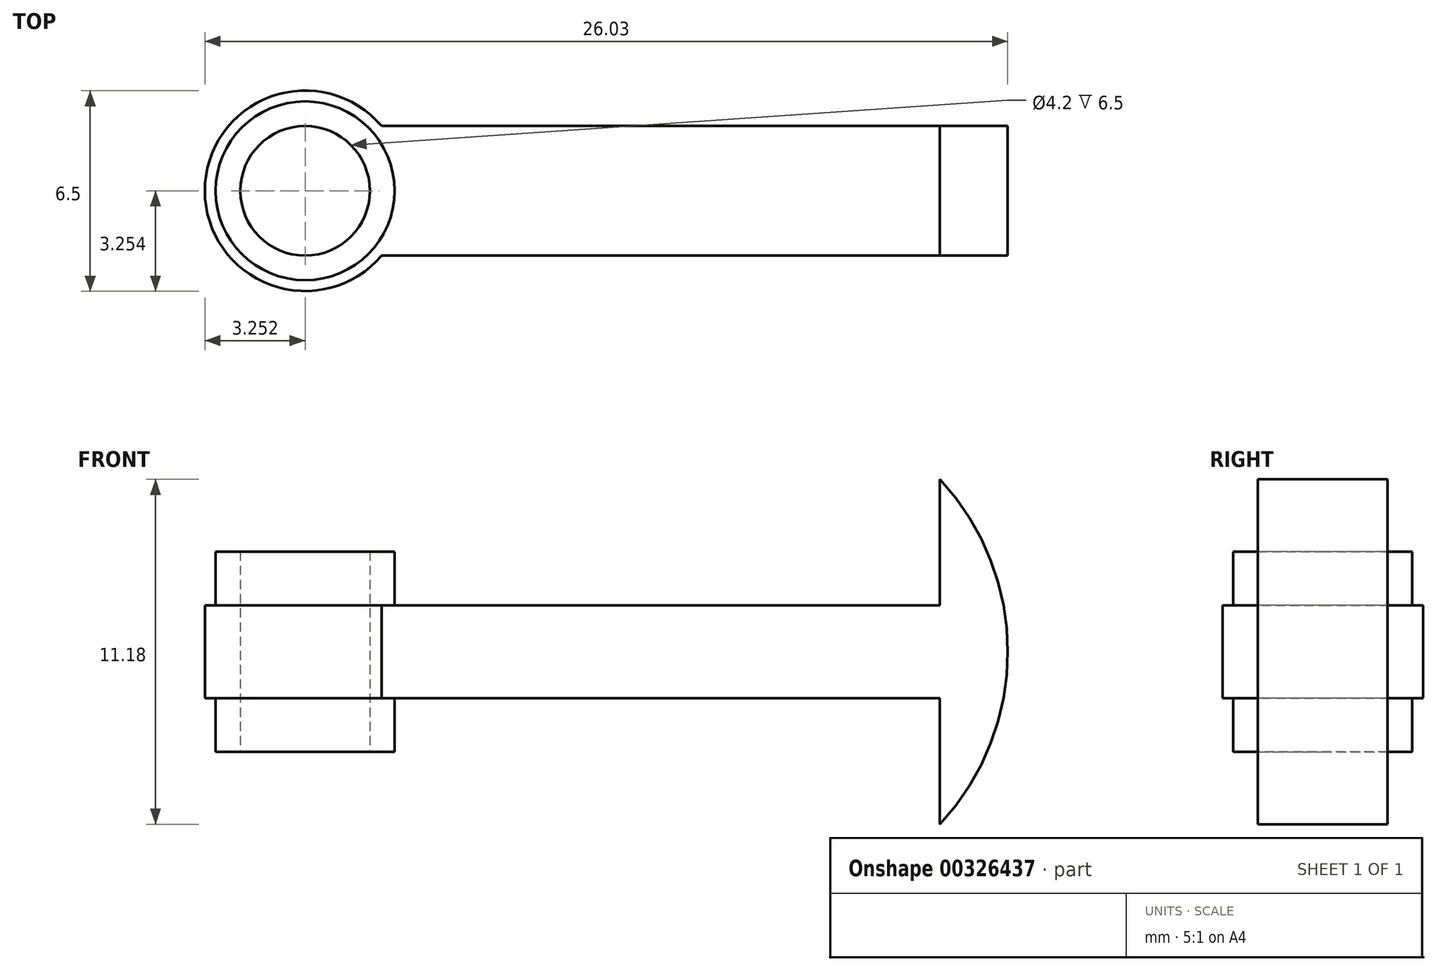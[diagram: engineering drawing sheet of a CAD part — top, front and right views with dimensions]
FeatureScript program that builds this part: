
annotation { "Feature Type Name" : "Feature", "Feature Type Description" : "" }
export const myFeature = defineFeature(function(context is Context, id is Id, definition is map)
    precondition{}
    {
        {
            var Q0;
            Q0=qCreatedBy(makeId("Top.planeOp"),FACE);
            var sketch = newSketch(context, id + "F0", { "sketchPlane" : qUnion([Q0])});
            skLineSegment(sketch, "E0.right", {"start": v(10.92, 10.5) * mm, "end": v(10.92, 8.1) * mm});
            skPoint(sketch, "E1", {"position": v(-5.16, 1.5) * mm});
            skPoint(sketch, "E2", {"position": v(-9.66, 6) * mm});
            skCircle(sketch, "E3", {"center": v(-9.66, 6) * mm, "radius": 2.1 * mm});
            skArc(sketch, "E4", {"start": v(-7.18, 8.1) * mm, "mid": v(-12.9, 6) * mm, "end": v(-7.18, 3.9) * mm});
            skLineSegment(sketch, "E5", {"start": v(-7.18, 8.1) * mm, "end": v(10.92, 8.1) * mm});
            skLineSegment(sketch, "E6", {"start": v(-7.18, 3.9) * mm, "end": v(10.92, 3.9) * mm});
            skPoint(sketch, "E0.left.start.orphan", {"position": v(-14.16, 10.5) * mm});
            skPoint(sketch, "E7.orphan", {"position": v(-14.16, 1.5) * mm});
            skLineSegment(sketch, "E8.bottom", {"start": v(10.92, 10.5) * mm, "end": v(18.8, 10.5) * mm});
            skLineSegment(sketch, "E8.top", {"start": v(10.92, 1.5) * mm, "end": v(18.8, 1.5) * mm});
            skLineSegment(sketch, "E8.right", {"start": v(18.8, 10.5) * mm, "end": v(18.8, 1.5) * mm});
            skLineSegment(sketch, "E9.trimOffspring", {"start": v(10.92, 3.9) * mm, "end": v(10.92, 1.5) * mm});
            skLineSegment(sketch, "E10", {"start": v(10.92, 8.1) * mm, "end": v(10.92, 3.9) * mm});
            skSolve(sketch);
        }
        {
            var Q0;
            Q0=makeQuery(id+"F0.imprint","IMPRINT",FACE,{"disambiguationData":[TD([[makeQuery(id+"F0.imprint","IMPRINT",EDGE,{"derivedFrom":sQuery(id+"F0.wireOp",EDGE,"E0.right")}),1.0]])]});
            var Q1;
            Q1=makeQuery(id+"F0.imprint","IMPRINT",FACE,{"disambiguationData":[TD([[makeQuery(id+"F0.imprint","IMPRINT",EDGE,{"derivedFrom":sQuery(id+"F0.wireOp",EDGE,"E3")}),-1.0]])]});
            extrude(context, id + "F1", {"entities" : qUnion([Q0, Q1]), "depth" : 3 * mm});
        }
        {
            var Q0;
            Q0=makeQuery(id+"F1.opExtrude","CAP_FACE",FACE,{"disambiguationData":[OSD([sQuery(id+"F0.wireOp",EDGE,"E0.right"),sQuery(id+"F0.wireOp",EDGE,"E3"),sQuery(id+"F0.wireOp",EDGE,"E4"),sQuery(id+"F0.wireOp",EDGE,"E5"),sQuery(id+"F0.wireOp",EDGE,"E6"),sQuery(id+"F0.wireOp",EDGE,"E8.bottom"),sQuery(id+"F0.wireOp",EDGE,"E8.top"),sQuery(id+"F0.wireOp",EDGE,"E8.right"),sQuery(id+"F0.wireOp",EDGE,"E9.trimOffspring")])],"isStart":false});
            var sketch = newSketch(context, id + "F2", { "sketchPlane" : qUnion([Q0])});
            skPoint(sketch, "E11", {"position": v(9.92, 10.5) * mm});
            skLineSegment(sketch, "E12", {"start": v(10.92, 8.1) * mm, "end": v(10.92, 3.9) * mm});
            skLineSegment(sketch, "E13", {"start": v(10.92, 3.9) * mm, "end": v(18.8, 3.9) * mm});
            skLineSegment(sketch, "E14", {"start": v(10.92, 8.1) * mm, "end": v(18.8, 8.1) * mm});
            skSolve(sketch);
        }
        {
            var Q0;
            {var subQ0=sQuery(id+"F2.wireOp",EDGE,"E14");Q0=makeQuery(id+"F2.imprint","IMPRINT",FACE,{"disambiguationData":[TD([[makeQuery(id+"F2.imprint","IMPRINT",EDGE,{"derivedFrom":subQ0}),1.0]])]});}
            var Q1;
            {var subQ0=sQuery(id+"F2.wireOp",EDGE,"E13");Q1=makeQuery(id+"F2.imprint","IMPRINT",FACE,{"disambiguationData":[TD([[makeQuery(id+"F2.imprint","IMPRINT",EDGE,{"derivedFrom":subQ0}),-1.0]])]});}
            extrude(context, id + "F3", {"entities" : qUnion([Q0, Q1]), "operationType" : NewBodyOperationType.REMOVE, "oppositeDirection" : true, "depth" : 25 * mm});
        }
        {
            var Q0;
            Q0=makeQuery(id+"F2.imprint","IMPRINT",FACE,{"disambiguationData":[TD([[makeQuery(id+"F2.imprint","IMPRINT",EDGE,{"derivedFrom":sQuery(id+"F2.wireOp",EDGE,"E12")}),1.0]])]});
            extrude(context, id + "F4", {"entities" : qUnion([Q0]), "operationType" : NewBodyOperationType.ADD, "depth" : 5 * mm});
        }
        {
            var Q0;
            Q0=makeQuery(id+"F2.imprint","IMPRINT",FACE,{"disambiguationData":[TD([[makeQuery(id+"F2.imprint","IMPRINT",EDGE,{"derivedFrom":sQuery(id+"F2.wireOp",EDGE,"E12")}),1.0]])]});
            extrude(context, id + "F5", {"entities" : qUnion([Q0]), "operationType" : NewBodyOperationType.ADD, "oppositeDirection" : true, "depth" : 8 * mm});
        }
        {
            var Q0;
            {var subQ0=sQuery(id+"F2.wireOp",EDGE,"E14");Q0=makeQuery(id+"F5.boolean.opBoolean","MERGE",FACE,{"derivedFrom":[makeQuery(id+"F4.boolean.opBoolean","MERGE",FACE,{"derivedFrom":[makeQuery(id+"F3.boolean.opBoolean","MERGE",FACE,{"derivedFrom":[makeQuery(id+"F1.opExtrude","SWEPT_FACE",FACE,{"disambiguationData":[OSD([sQuery(id+"F0.wireOp",EDGE,"E5")])]}),makeQuery(id+"F3.opExtrude","SWEPT_FACE",FACE,{"disambiguationData":[OSD([subQ0])]})]}),makeQuery(id+"F4.opExtrude","SWEPT_FACE",FACE,{"disambiguationData":[OSD([subQ0])]})]}),makeQuery(id+"F5.opExtrude","SWEPT_FACE",FACE,{"disambiguationData":[OSD([subQ0])]})]});}
            var sketch = newSketch(context, id + "F6", { "sketchPlane" : qUnion([Q0])});
            skPoint(sketch, "E15", {"position": v(-9.92, 8) * mm});
            skLineSegment(sketch, "E16", {"start": v(-9.92, 8) * mm, "end": v(-9.92, -5) * mm, "construction": true});
            skArc(sketch, "E17", {"start": v(-9.92, 8) * mm, "mid": v(-13.12, 1.5) * mm, "end": v(-9.92, -5) * mm});
            skSolve(sketch);
        }
        {
            var Q0;
            {var subQ0=sQuery(id+"F6.wireOp",EDGE,"E17");Q0=makeQuery(id+"F6.imprint","IMPRINT",FACE,{"disambiguationData":[TD([[makeQuery(id+"F6.imprint","IMPRINT",EDGE,{"derivedFrom":subQ0}),-1.0]])]});}
            extrude(context, id + "F7", {"entities" : qUnion([Q0]), "operationType" : NewBodyOperationType.REMOVE, "oppositeDirection" : true, "depth" : 25 * mm});
        }
        {
            var Q0;
            Q0=makeQuery(id+"F1.opExtrude","CAP_FACE",FACE,{"disambiguationData":[OSD([sQuery(id+"F0.wireOp",EDGE,"E0.right"),sQuery(id+"F0.wireOp",EDGE,"E3"),sQuery(id+"F0.wireOp",EDGE,"E4"),sQuery(id+"F0.wireOp",EDGE,"E5"),sQuery(id+"F0.wireOp",EDGE,"E6"),sQuery(id+"F0.wireOp",EDGE,"E8.bottom"),sQuery(id+"F0.wireOp",EDGE,"E8.top"),sQuery(id+"F0.wireOp",EDGE,"E8.right"),sQuery(id+"F0.wireOp",EDGE,"E9.trimOffspring")])],"isStart":true});
            var sketch = newSketch(context, id + "F8", { "sketchPlane" : qUnion([Q0])});
            skPoint(sketch, "E18", {"position": v(-9.66, -6) * mm});
            skCircle(sketch, "E19", {"center": v(-9.66, -6) * mm, "radius": 2.9 * mm});
            skSolve(sketch);
        }
        {
            var Q0;
            Q0=makeQuery(id+"F8.imprint","IMPRINT",FACE,{"disambiguationData":[TD([[makeQuery(id+"F8.imprint","IMPRINT",EDGE,{"derivedFrom":sQuery(id+"F8.wireOp",EDGE,"E19")}),1.0]])]});
            extrude(context, id + "F9", {"entities" : qUnion([Q0]), "operationType" : NewBodyOperationType.ADD, "depth" : 1.75 * mm});
        }
        {
            var Q0;
            Q0=makeQuery(id+"F1.opExtrude","CAP_FACE",FACE,{"disambiguationData":[OSD([sQuery(id+"F0.wireOp",EDGE,"E0.right"),sQuery(id+"F0.wireOp",EDGE,"E3"),sQuery(id+"F0.wireOp",EDGE,"E4"),sQuery(id+"F0.wireOp",EDGE,"E5"),sQuery(id+"F0.wireOp",EDGE,"E6"),sQuery(id+"F0.wireOp",EDGE,"E8.bottom"),sQuery(id+"F0.wireOp",EDGE,"E8.top"),sQuery(id+"F0.wireOp",EDGE,"E8.right"),sQuery(id+"F0.wireOp",EDGE,"E9.trimOffspring")])],"isStart":false});
            var sketch = newSketch(context, id + "F10", { "sketchPlane" : qUnion([Q0])});
            skPoint(sketch, "E20", {"position": v(-9.66, 6) * mm});
            skCircle(sketch, "E21", {"center": v(-9.66, 6) * mm, "radius": 2.9 * mm});
            skSolve(sketch);
        }
        {
            var Q0;
            Q0=makeQuery(id+"F10.imprint","IMPRINT",FACE,{"disambiguationData":[TD([[makeQuery(id+"F10.imprint","IMPRINT",EDGE,{"derivedFrom":sQuery(id+"F10.wireOp",EDGE,"E21")}),1.0]])]});
            extrude(context, id + "F11", {"entities" : qUnion([Q0]), "operationType" : NewBodyOperationType.ADD, "depth" : 1.75 * mm});
        }
    });
